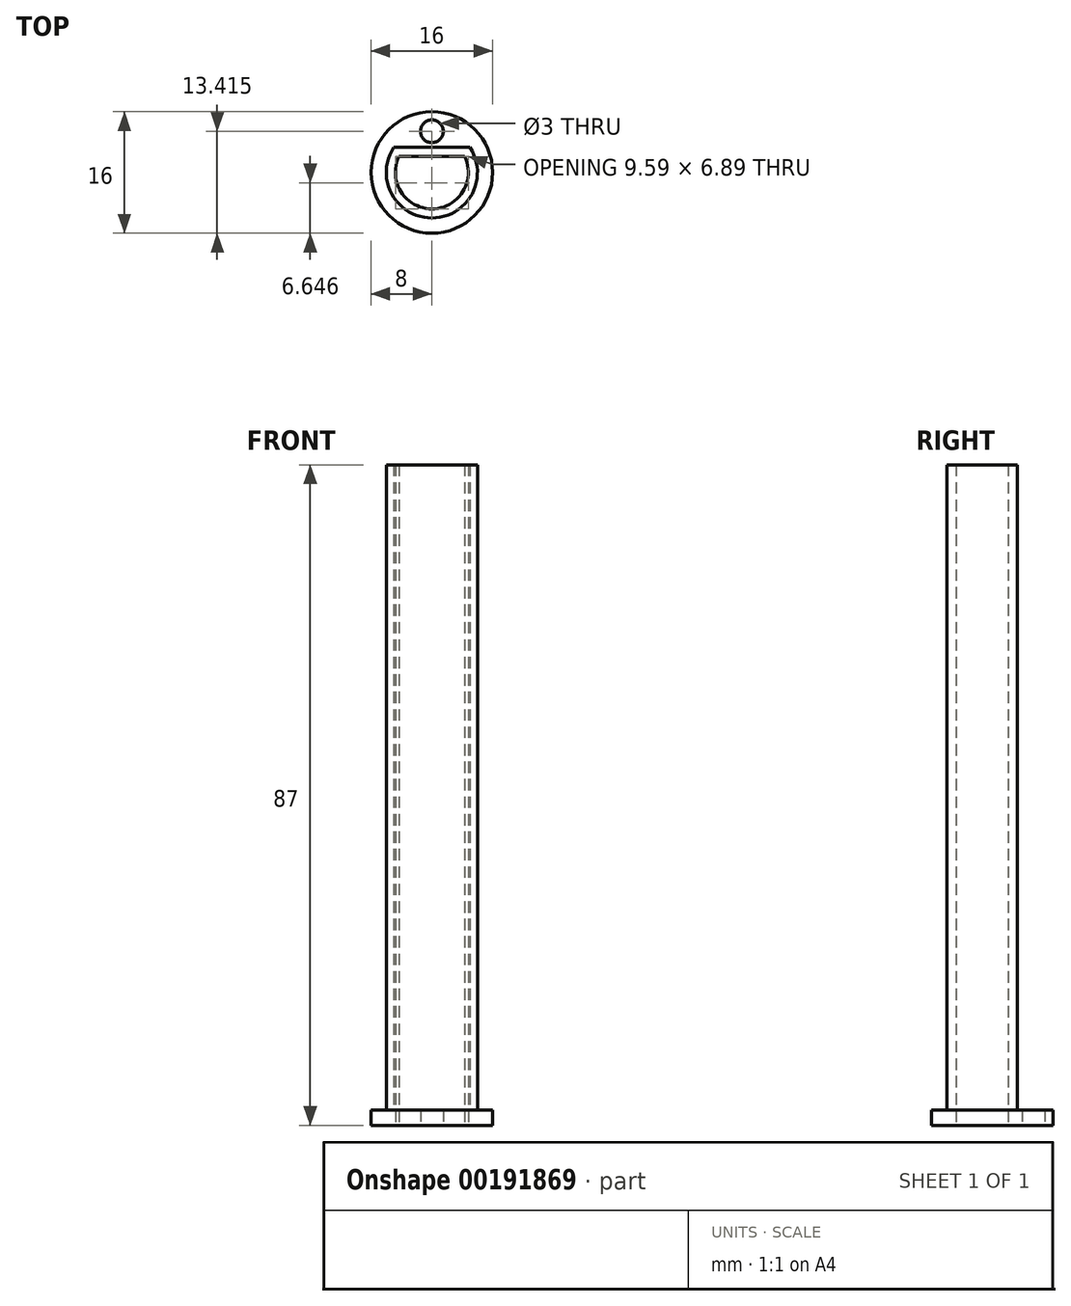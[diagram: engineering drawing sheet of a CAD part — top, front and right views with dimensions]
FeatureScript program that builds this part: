
annotation { "Feature Type Name" : "Feature", "Feature Type Description" : "" }
export const myFeature = defineFeature(function(context is Context, id is Id, definition is map)
    precondition{}
    {
        {
            var Q0;
            Q0=qCreatedBy(makeId("Top.planeOp"),FACE);
            var sketch = newSketch(context, id + "F0", { "sketchPlane" : qUnion([Q0])});
            skArc(sketch, "E0", {"start": v(-5.02, 3.3) * mm, "mid": v(0, -6) * mm, "end": v(5.02, 3.3) * mm});
            skCircle(sketch, "E1", {"center": v(0, 0) * mm, "radius": 8 * mm});
            skLineSegment(sketch, "E2", {"start": v(-5.02, 3.3) * mm, "end": v(5.02, 3.3) * mm});
            skLineSegment(sketch, "E3.0", {"start": v(-4.32, 2.1) * mm, "end": v(4.32, 2.1) * mm});
            skArc(sketch, "E3.1", {"start": v(-4.32, 2.1) * mm, "mid": v(0, -4.8) * mm, "end": v(4.32, 2.1) * mm});
            skCircle(sketch, "E4", {"center": v(0, 5.42) * mm, "radius": 1.5 * mm});
            skSolve(sketch);
        }
        {
            var Q0;
            Q0=makeQuery(id+"F0.imprint","IMPRINT",FACE,{"disambiguationData":[TD([[makeQuery(id+"F0.imprint","IMPRINT",EDGE,{"derivedFrom":sQuery(id+"F0.wireOp",EDGE,"E0")}),1.0]])]});
            extrude(context, id + "F1", {"entities" : qUnion([Q0]), "depth" : 87 * mm});
        }
        {
            var Q0;
            Q0=makeQuery(id+"F0.imprint","IMPRINT",FACE,{"disambiguationData":[TD([[makeQuery(id+"F0.imprint","IMPRINT",EDGE,{"derivedFrom":sQuery(id+"F0.wireOp",EDGE,"E0")}),-1.0]])]});
            extrude(context, id + "F2", {"entities" : qUnion([Q0]), "operationType" : NewBodyOperationType.ADD, "depth" : 2 * mm});
        }
    });
